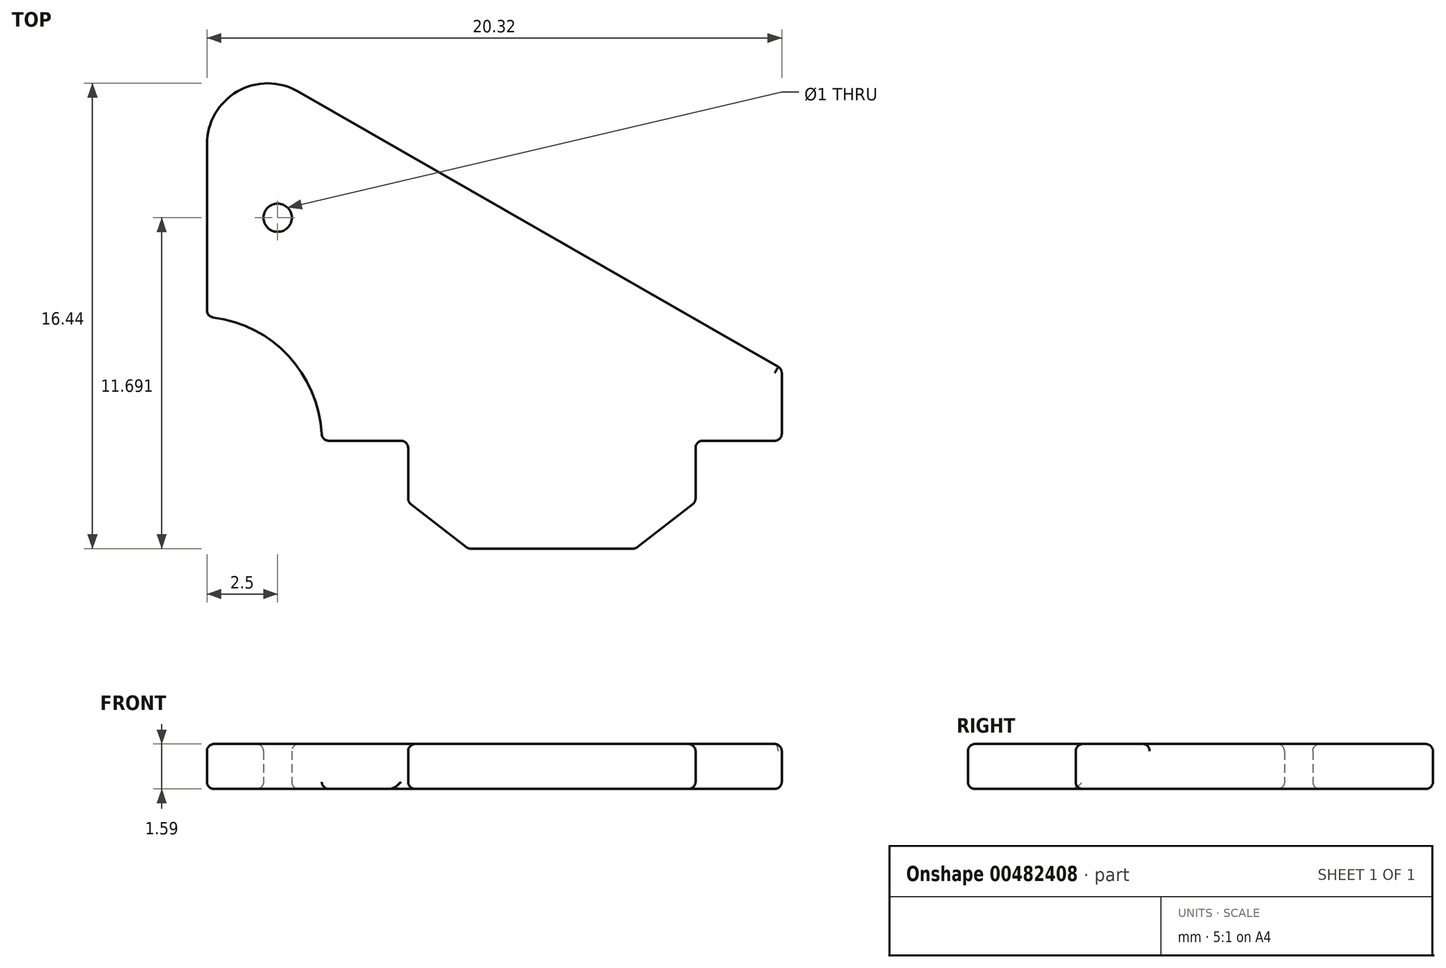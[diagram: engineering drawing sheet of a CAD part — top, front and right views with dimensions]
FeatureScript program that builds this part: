
annotation { "Feature Type Name" : "Feature", "Feature Type Description" : "" }
export const myFeature = defineFeature(function(context is Context, id is Id, definition is map)
    precondition{}
    {
        {
            var Q0;
            Q0=qCreatedBy(makeId("Top.planeOp"),FACE);
            var sketch = newSketch(context, id + "F0", { "sketchPlane" : qUnion([Q0])});
            skLineSegment(sketch, "E0", {"start": v(-16.26, 0) * mm, "end": v(-13.2, 0) * mm});
            skLineSegment(sketch, "E1", {"start": v(-13.2, 0) * mm, "end": v(-13.2, -2.16) * mm});
            skLineSegment(sketch, "E2", {"start": v(-13.2, -2.16) * mm, "end": v(-11.08, -3.8) * mm});
            skLineSegment(sketch, "E3", {"start": v(-11.08, -3.81) * mm, "end": v(-5.18, -3.81) * mm});
            skLineSegment(sketch, "E4", {"start": v(-5.18, -3.81) * mm, "end": v(-3.05, -2.16) * mm});
            skLineSegment(sketch, "E5", {"start": v(-3.05, -2.16) * mm, "end": v(-3.05, 0) * mm});
            skLineSegment(sketch, "E6", {"start": v(-3.05, 0) * mm, "end": v(0, 0) * mm});
            skLineSegment(sketch, "E7", {"start": v(0, 0) * mm, "end": v(0, 2.54) * mm});
            skLineSegment(sketch, "E8", {"start": v(0, 2.54) * mm, "end": v(-17.1, 12.34) * mm});
            skLineSegment(sketch, "E9", {"start": v(-20.32, 10.48) * mm, "end": v(-20.32, 4.38) * mm});
            skArc(sketch, "E10", {"start": v(-16.26, 0) * mm, "mid": v(-17.43, 2.99) * mm, "end": v(-20.32, 4.38) * mm});
            skArc(sketch, "E11.filletArc", {"start": v(-17.1, 12.34) * mm, "mid": v(-19.25, 12.34) * mm, "end": v(-20.32, 10.48) * mm});
            skCircle(sketch, "E12", {"center": v(-17.82, 7.88) * mm, "radius": 0.5 * mm});
            skSolve(sketch);
        }
        {
            var Q0;
            Q0 = qSketchRegion(id + "F0", true);
            extrude(context, id + "F1", {"entities" : qUnion([Q0]), "depth" : 1.59 * mm});
        }
        {
            var Q0;
            Q0=makeQuery(id+"F1.opExtrude","CAP_EDGE",EDGE,{"disambiguationData":[OSD([sQuery(id+"F0.wireOp",EDGE,"E9")])],"isStart":false});
            var Q1;
            Q1=makeQuery(id+"F1.opExtrude","CAP_EDGE",EDGE,{"disambiguationData":[OSD([sQuery(id+"F0.wireOp",EDGE,"E11.filletArc")])],"isStart":false});
            var Q2;
            Q2=makeQuery(id+"F1.opExtrude","CAP_EDGE",EDGE,{"disambiguationData":[OSD([sQuery(id+"F0.wireOp",EDGE,"E8")])],"isStart":false});
            var Q3;
            Q3=makeQuery(id+"F1.opExtrude","CAP_EDGE",EDGE,{"disambiguationData":[OSD([sQuery(id+"F0.wireOp",EDGE,"E7")])],"isStart":false});
            var Q4;
            Q4=makeQuery(id+"F1.opExtrude","CAP_EDGE",EDGE,{"disambiguationData":[OSD([sQuery(id+"F0.wireOp",EDGE,"E6")])],"isStart":false});
            var Q5;
            Q5=makeQuery(id+"F1.opExtrude","CAP_EDGE",EDGE,{"disambiguationData":[OSD([sQuery(id+"F0.wireOp",EDGE,"E5")])],"isStart":false});
            var Q6;
            Q6=makeQuery(id+"F1.opExtrude","CAP_EDGE",EDGE,{"disambiguationData":[OSD([sQuery(id+"F0.wireOp",EDGE,"E4")])],"isStart":false});
            var Q7;
            Q7=makeQuery(id+"F1.opExtrude","CAP_EDGE",EDGE,{"disambiguationData":[OSD([sQuery(id+"F0.wireOp",EDGE,"E3")])],"isStart":false});
            var Q8;
            Q8=makeQuery(id+"F1.opExtrude","CAP_EDGE",EDGE,{"disambiguationData":[OSD([sQuery(id+"F0.wireOp",EDGE,"E2")])],"isStart":false});
            var Q9;
            Q9=makeQuery(id+"F1.opExtrude","CAP_EDGE",EDGE,{"disambiguationData":[OSD([sQuery(id+"F0.wireOp",EDGE,"E1")])],"isStart":false});
            var Q10;
            Q10=makeQuery(id+"F1.opExtrude","CAP_EDGE",EDGE,{"disambiguationData":[OSD([sQuery(id+"F0.wireOp",EDGE,"E0")])],"isStart":false});
            var Q11;
            Q11=makeQuery(id+"F1.opExtrude","CAP_EDGE",EDGE,{"disambiguationData":[OSD([sQuery(id+"F0.wireOp",EDGE,"E10")])],"isStart":false});
            var Q12;
            Q12=makeQuery(id+"F1.opExtrude","CAP_EDGE",EDGE,{"disambiguationData":[OSD([sQuery(id+"F0.wireOp",EDGE,"E10")])],"isStart":true});
            var Q13;
            Q13=makeQuery(id+"F1.opExtrude","SWEPT_EDGE",EDGE,{"disambiguationData":[OSD([sQuery(id+"F0.wireOp",EDGE,"E9"),sQuery(id+"F0.wireOp",EDGE,"E10")])]});
            var Q14;
            Q14=makeQuery(id+"F1.opExtrude","SWEPT_EDGE",EDGE,{"disambiguationData":[OSD([sQuery(id+"F0.wireOp",EDGE,"E6"),sQuery(id+"F0.wireOp",EDGE,"E7")])]});
            var Q15;
            Q15=makeQuery(id+"F1.opExtrude","SWEPT_EDGE",EDGE,{"disambiguationData":[OSD([sQuery(id+"F0.wireOp",EDGE,"E7"),sQuery(id+"F0.wireOp",EDGE,"E8")])]});
            var Q16;
            Q16=makeQuery(id+"F1.opExtrude","SWEPT_EDGE",EDGE,{"disambiguationData":[OSD([sQuery(id+"F0.wireOp",EDGE,"E5"),sQuery(id+"F0.wireOp",EDGE,"E6")])]});
            var Q17;
            Q17=makeQuery(id+"F1.opExtrude","SWEPT_EDGE",EDGE,{"disambiguationData":[OSD([sQuery(id+"F0.wireOp",EDGE,"E4"),sQuery(id+"F0.wireOp",EDGE,"E5")])]});
            var Q18;
            Q18=makeQuery(id+"F1.opExtrude","SWEPT_EDGE",EDGE,{"disambiguationData":[OSD([sQuery(id+"F0.wireOp",EDGE,"E3"),sQuery(id+"F0.wireOp",EDGE,"E4")])]});
            var Q19;
            Q19=makeQuery(id+"F1.opExtrude","SWEPT_EDGE",EDGE,{"disambiguationData":[OSD([sQuery(id+"F0.wireOp",EDGE,"E2"),sQuery(id+"F0.wireOp",EDGE,"E3")])]});
            var Q20;
            Q20=makeQuery(id+"F1.opExtrude","SWEPT_EDGE",EDGE,{"disambiguationData":[OSD([sQuery(id+"F0.wireOp",EDGE,"E1"),sQuery(id+"F0.wireOp",EDGE,"E2")])]});
            var Q21;
            Q21=makeQuery(id+"F1.opExtrude","CAP_EDGE",EDGE,{"disambiguationData":[OSD([sQuery(id+"F0.wireOp",EDGE,"E9")])],"isStart":true});
            var Q22;
            Q22=makeQuery(id+"F1.opExtrude","CAP_EDGE",EDGE,{"disambiguationData":[OSD([sQuery(id+"F0.wireOp",EDGE,"E11.filletArc")])],"isStart":true});
            var Q23;
            Q23=makeQuery(id+"F1.opExtrude","CAP_EDGE",EDGE,{"disambiguationData":[OSD([sQuery(id+"F0.wireOp",EDGE,"E8")])],"isStart":true});
            var Q24;
            Q24=makeQuery(id+"F1.opExtrude","CAP_EDGE",EDGE,{"disambiguationData":[OSD([sQuery(id+"F0.wireOp",EDGE,"E7")])],"isStart":true});
            var Q25;
            Q25=makeQuery(id+"F1.opExtrude","CAP_EDGE",EDGE,{"disambiguationData":[OSD([sQuery(id+"F0.wireOp",EDGE,"E1")])],"isStart":true});
            var Q26;
            Q26=makeQuery(id+"F1.opExtrude","CAP_EDGE",EDGE,{"disambiguationData":[OSD([sQuery(id+"F0.wireOp",EDGE,"E2")])],"isStart":true});
            var Q27;
            Q27=makeQuery(id+"F1.opExtrude","CAP_EDGE",EDGE,{"disambiguationData":[OSD([sQuery(id+"F0.wireOp",EDGE,"E3")])],"isStart":true});
            var Q28;
            Q28=makeQuery(id+"F1.opExtrude","CAP_EDGE",EDGE,{"disambiguationData":[OSD([sQuery(id+"F0.wireOp",EDGE,"E4")])],"isStart":true});
            var Q29;
            Q29=makeQuery(id+"F1.opExtrude","CAP_EDGE",EDGE,{"disambiguationData":[OSD([sQuery(id+"F0.wireOp",EDGE,"E5")])],"isStart":true});
            var Q30;
            Q30=makeQuery(id+"F1.opExtrude","CAP_EDGE",EDGE,{"disambiguationData":[OSD([sQuery(id+"F0.wireOp",EDGE,"E6")])],"isStart":true});
            var Q31;
            Q31=makeQuery(id+"F1.opExtrude","SWEPT_EDGE",EDGE,{"disambiguationData":[OSD([sQuery(id+"F0.wireOp",EDGE,"E0"),sQuery(id+"F0.wireOp",EDGE,"E10")])]});
            var Q32;
            Q32=makeQuery(id+"F1.opExtrude","SWEPT_EDGE",EDGE,{"disambiguationData":[OSD([sQuery(id+"F0.wireOp",EDGE,"E0"),sQuery(id+"F0.wireOp",EDGE,"E1")])]});
            var Q33;
            Q33=makeQuery(id+"F1.opExtrude","CAP_EDGE",EDGE,{"disambiguationData":[OSD([sQuery(id+"F0.wireOp",EDGE,"E12")])],"isStart":false});
            var Q34;
            Q34=makeQuery(id+"F1.opExtrude","CAP_EDGE",EDGE,{"disambiguationData":[OSD([sQuery(id+"F0.wireOp",EDGE,"E12")])],"isStart":true});
            fillet(context, id + "F2", {"entities" : qUnion([Q0, Q1, Q2, Q3, Q4, Q5, Q6, Q7, Q8, Q9, Q10, Q11, Q12, Q13, Q14, Q15, Q16, Q17, Q18, Q19, Q20, Q21, Q22, Q23, Q24, Q25, Q26, Q27, Q28, Q29, Q30, Q31, Q32, Q33, Q34]), "radius" : 0.25 * mm, "tangentPropagation" : true, "allowEdgeOverflow" : false});
        }
    });
